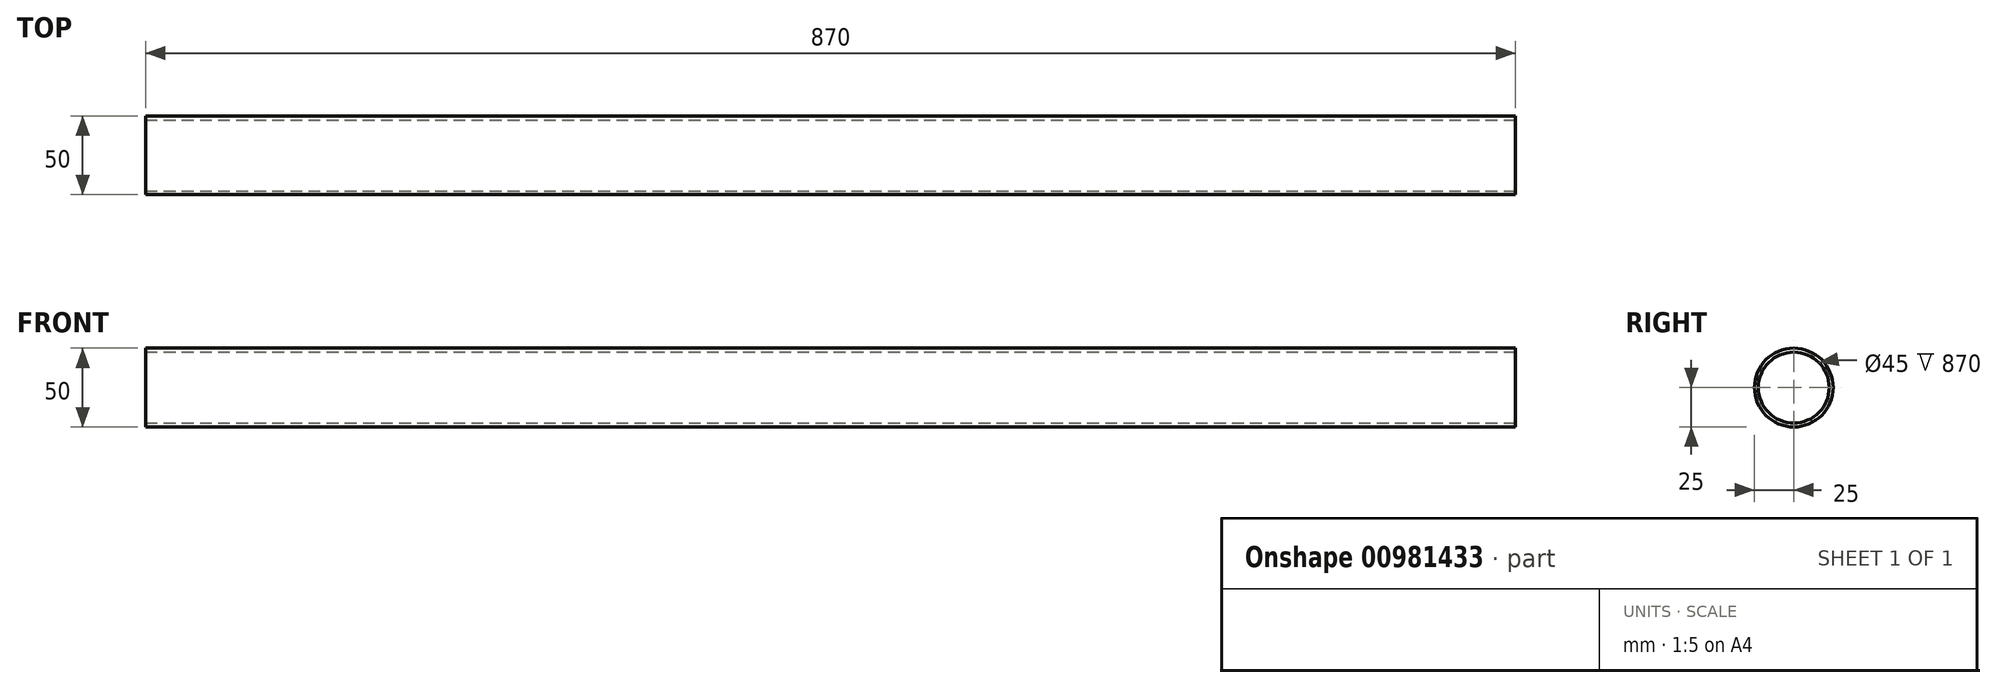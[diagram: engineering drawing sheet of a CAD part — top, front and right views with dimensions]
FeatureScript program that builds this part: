
annotation { "Feature Type Name" : "Feature", "Feature Type Description" : "" }
export const myFeature = defineFeature(function(context is Context, id is Id, definition is map)
    precondition{}
    {
        {
            var Q0;
            Q0=qCreatedBy(makeId("Front.planeOp"),FACE);
            var sketch = newSketch(context, id + "F0", { "sketchPlane" : qUnion([Q0])});
            skLineSegment(sketch, "E0.bottom", {"start": v(-435, 25) * mm, "end": v(435, 25) * mm});
            skLineSegment(sketch, "E0.top", {"start": v(-435, -25) * mm, "end": v(435, -25) * mm});
            skLineSegment(sketch, "E0.left", {"start": v(-435, 25) * mm, "end": v(-435, -25) * mm});
            skLineSegment(sketch, "E0.right", {"start": v(435, 25) * mm, "end": v(435, -25) * mm});
            skPoint(sketch, "E0.middle", {"position": v(0, 0) * mm});
            skSolve(sketch);
        }
        {
            var Q0;
            Q0 = qSketchRegion(id + "F0", true);
            extrude(context, id + "F1", {"entities" : qUnion([Q0]), "depth" : 50 * mm, "offsetDistance" : 25 * mm});
        }
        {
            var Q0;
            Q0=makeQuery(id+"F1.opExtrude","CAP_EDGE",EDGE,{"disambiguationData":[OSD([sQuery(id+"F0.wireOp",EDGE,"E0.top")])],"isStart":false});
            var Q1;
            Q1=makeQuery(id+"F1.opExtrude","CAP_EDGE",EDGE,{"disambiguationData":[OSD([sQuery(id+"F0.wireOp",EDGE,"E0.top")])],"isStart":true});
            var Q2;
            Q2=makeQuery(id+"F1.opExtrude","CAP_EDGE",EDGE,{"disambiguationData":[OSD([sQuery(id+"F0.wireOp",EDGE,"E0.bottom")])],"isStart":true});
            var Q3;
            Q3=makeQuery(id+"F1.opExtrude","CAP_EDGE",EDGE,{"disambiguationData":[OSD([sQuery(id+"F0.wireOp",EDGE,"E0.bottom")])],"isStart":false});
            fillet(context, id + "F2", {"entities" : qUnion([Q0, Q1, Q2, Q3]), "radius" : 25 * mm, "tangentPropagation" : true, "allowEdgeOverflow" : false});
        }
        {
            var Q0;
            Q0=makeQuery(id+"F1.opExtrude","SWEPT_FACE",FACE,{"disambiguationData":[OSD([sQuery(id+"F0.wireOp",EDGE,"E0.left")])]});
            var Q1;
            Q1=makeQuery(id+"F1.opExtrude","SWEPT_FACE",FACE,{"disambiguationData":[OSD([sQuery(id+"F0.wireOp",EDGE,"E0.right")])]});
            shell(context, id + "F3", {"entities" : qUnion([Q0, Q1]), "thickness" : 2.5 * mm});
        }
    });
